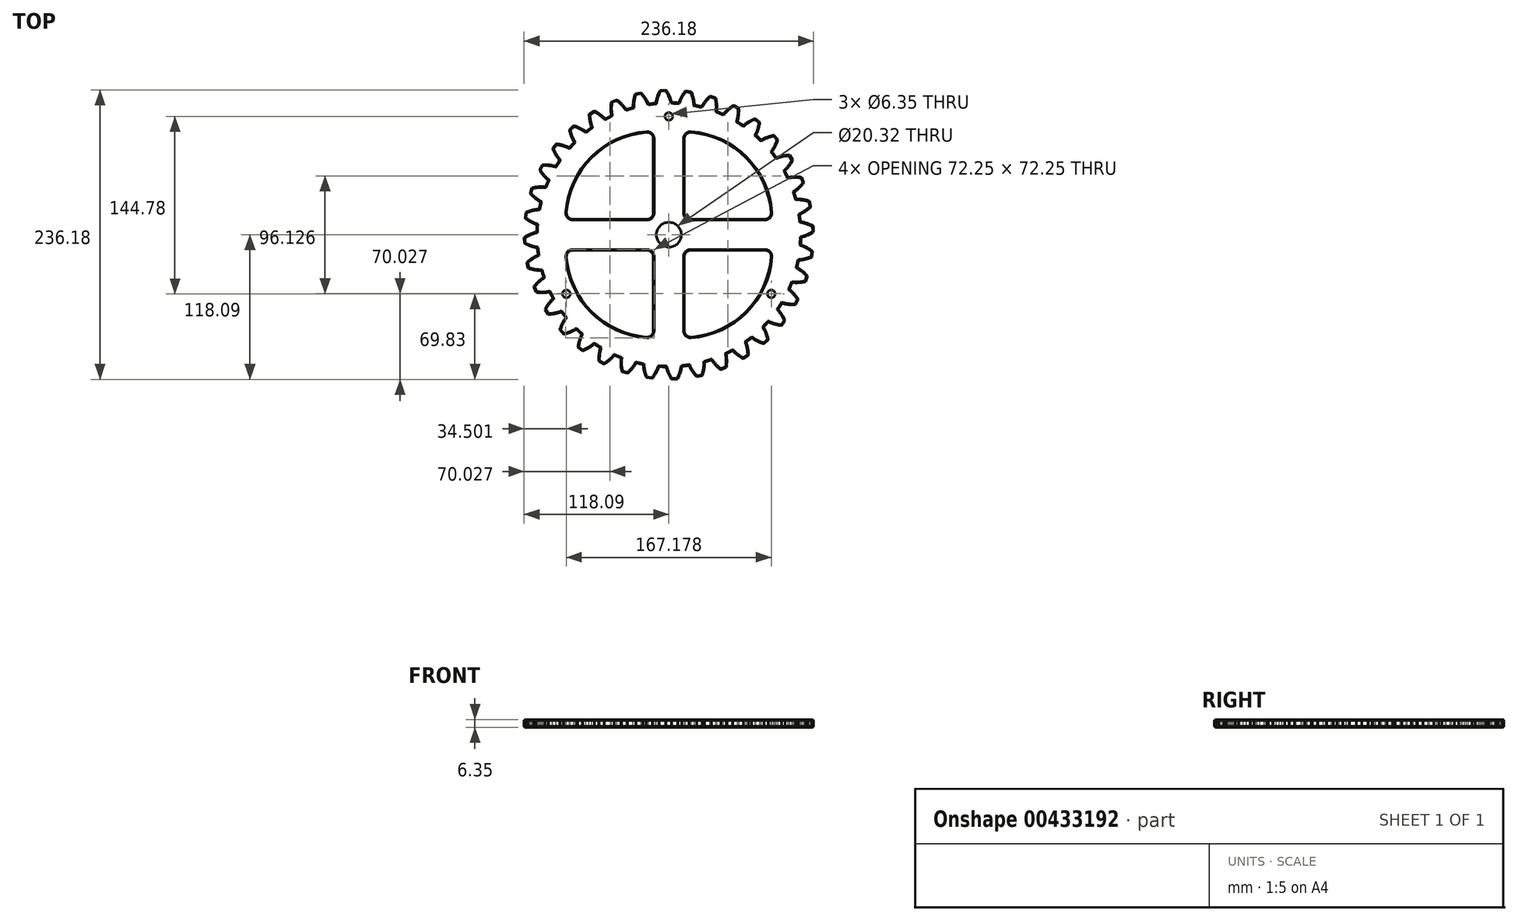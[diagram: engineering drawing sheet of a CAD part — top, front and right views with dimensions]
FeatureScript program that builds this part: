
annotation { "Feature Type Name" : "Feature", "Feature Type Description" : "" }
export const myFeature = defineFeature(function(context is Context, id is Id, definition is map)
    precondition{}
    {
        {
            var Q0;
            Q0=qCreatedBy(makeId("Top.planeOp"),FACE);
            var sketch = newSketch(context, id + "F0", { "sketchPlane" : qUnion([Q0])});
            skCircle(sketch, "E0", {"center": v(0, 0) * mm, "radius": 30.48 * mm, "construction": true});
            skSolve(sketch);
        }
        {
            var Q0;
            Q0=qCreatedBy(makeId("Top.planeOp"),FACE);
            var sketch = newSketch(context, id + "F1", { "sketchPlane" : qUnion([Q0])});
            skCircle(sketch, "E1", {"center": v(0, 0) * mm, "radius": 118.11 * mm, "construction": true});
            skCircle(sketch, "E2", {"center": v(0, 0) * mm, "radius": 114.3 * mm, "construction": true});
            skCircle(sketch, "E3", {"center": v(0, 0) * mm, "radius": 107.95 * mm, "construction": true});
            skLineSegment(sketch, "E4", {"start": v(0, 0) * mm, "end": v(0, 56.9) * mm, "construction": true});
            skLineSegment(sketch, "E5", {"start": v(0, 0) * mm, "end": v(-2.3, 58.79) * mm, "construction": true});
            skLineSegment(sketch, "E6", {"start": v(0, 114.3) * mm, "end": v(-65.71, 114.3) * mm, "construction": true});
            skLineSegment(sketch, "E7", {"start": v(0, 114.3) * mm, "end": v(-58.85, 88.1) * mm, "construction": true});
            skCircle(sketch, "E8", {"center": v(0, 114.3) * mm, "radius": 31.75 * mm, "construction": true});
            skCircle(sketch, "E9", {"center": v(0, 0) * mm, "radius": 104.42 * mm, "construction": true});
            skCircle(sketch, "E10", {"center": v(-28.56, 100.44) * mm, "radius": 31.75 * mm, "construction": true});
            skArc(sketch, "E11", {"start": v(2.3, 107.93) * mm, "mid": v(0.5, 113.2) * mm, "end": v(-2.17, 118.09) * mm});
            skArc(sketch, "E12.MirrorCS", {"start": v(-10.75, 107.41) * mm, "mid": v(-9.39, 112.82) * mm, "end": v(-7.1, 117.9) * mm});
            skLineSegment(sketch, "E13", {"start": v(-7.1, 117.9) * mm, "end": v(-2.17, 118.09) * mm});
            skArc(sketch, "E14", {"start": v(-10.75, 107.41) * mm, "mid": v(4.24, -107.87) * mm, "end": v(2.3, 107.93) * mm});
            skSolve(sketch);
        }
        {
            var Q0;
            Q0=qSketchRegion(id+"F1",true);
            var Q1;
            Q1=makeQuery(id+"Ffi0VH93psu6soF_0.opExtrude","CAP_FACE",FACE,{"disambiguationData":[OSD([sQuery(id+"F0.wireOp",EDGE,"E0")])],"isStart":true});
            extrude(context, id + "F2", {"entities" : qUnion([Q0]), "oppositeDirection" : true, "endBoundEntityFace" : qUnion([Q1]), "depth" : 6.35 * mm});
        }
        {
            var Q0;
            Q0=makeQuery(id+"F2.opExtrude","SWEPT_BODY",BODY,{"disambiguationData":[OSD([sQuery(id+"F1.wireOp",EDGE,"E11"),sQuery(id+"F1.wireOp",EDGE,"E12.MirrorCS"),sQuery(id+"F1.wireOp",EDGE,"E13"),sQuery(id+"F1.wireOp",EDGE,"ZPE7Z8ba-rLlS-d3gG-Tl0h-fifcE816pJjn")])]});
            var Q1;
            Q1=sQuery(id+"F0.wireOp",EDGE,"E0");
            circularPattern(context, id + "F3", {"operationType" : NewBodyOperationType.ADD, "entities" : qUnion([Q0]), "axis" : qUnion([Q1]), "angle" : 360 * degree, "instanceCount" : 36, "equalSpace" : true});
        }
        {
            var Q0;
            {var subQ0=makeQuery(id+"F2.opExtrude","CAP_FACE",FACE,{"disambiguationData":[OSD([sQuery(id+"F1.wireOp",EDGE,"E11"),sQuery(id+"F1.wireOp",EDGE,"E12.MirrorCS"),sQuery(id+"F1.wireOp",EDGE,"E13"),sQuery(id+"F1.wireOp",EDGE,"ZPE7Z8ba-rLlS-d3gG-Tl0h-fifcE816pJjn")])],"isStart":true});Q0=makeQuery(id+"F3.boolean.opBoolean","MERGE",FACE,{"derivedFrom":[makeQuery(id+"Ffi0VH93psu6soF_0.opExtrude","CAP_FACE",FACE,{"disambiguationData":[OSD([sQuery(id+"F0.wireOp",EDGE,"E0")])],"isStart":false}),subQ0,makeQuery(id+"F3.opPattern","COPY",FACE,{"derivedFrom":subQ0,"instanceName":"1"}),makeQuery(id+"F3.opPattern","COPY",FACE,{"derivedFrom":subQ0,"instanceName":"2"}),makeQuery(id+"F3.opPattern","COPY",FACE,{"derivedFrom":subQ0,"instanceName":"3"}),makeQuery(id+"F3.opPattern","COPY",FACE,{"derivedFrom":subQ0,"instanceName":"4"}),makeQuery(id+"F3.opPattern","COPY",FACE,{"derivedFrom":subQ0,"instanceName":"5"}),makeQuery(id+"F3.opPattern","COPY",FACE,{"derivedFrom":subQ0,"instanceName":"6"}),makeQuery(id+"F3.opPattern","COPY",FACE,{"derivedFrom":subQ0,"instanceName":"7"}),makeQuery(id+"F3.opPattern","COPY",FACE,{"derivedFrom":subQ0,"instanceName":"8"}),makeQuery(id+"F3.opPattern","COPY",FACE,{"derivedFrom":subQ0,"instanceName":"9"}),makeQuery(id+"F3.opPattern","COPY",FACE,{"derivedFrom":subQ0,"instanceName":"10"}),makeQuery(id+"F3.opPattern","COPY",FACE,{"derivedFrom":subQ0,"instanceName":"11"}),makeQuery(id+"F3.opPattern","COPY",FACE,{"derivedFrom":subQ0,"instanceName":"12"}),makeQuery(id+"F3.opPattern","COPY",FACE,{"derivedFrom":subQ0,"instanceName":"13"}),makeQuery(id+"F3.opPattern","COPY",FACE,{"derivedFrom":subQ0,"instanceName":"14"})]});}
            var sketch = newSketch(context, id + "F4", { "sketchPlane" : qUnion([Q0])});
            skLineSegment(sketch, "E15", {"start": v(-12.7, 12.7) * mm, "end": v(-83.64, 12.7) * mm});
            skLineSegment(sketch, "E16", {"start": v(-12.7, 12.7) * mm, "end": v(-12.7, 83.64) * mm});
            skArc(sketch, "E17", {"start": v(-12.7, 83.64) * mm, "mid": v(-62.86, 62.86) * mm, "end": v(-83.64, 12.7) * mm});
            skArc(sketch, "E18.1.0", {"start": v(-83.64, -12.7) * mm, "mid": v(-62.86, -62.86) * mm, "end": v(-12.7, -83.64) * mm});
            skLineSegment(sketch, "E18.1.1", {"start": v(-12.7, -12.7) * mm, "end": v(-83.64, -12.7) * mm});
            skLineSegment(sketch, "E18.1.2", {"start": v(-12.7, -12.7) * mm, "end": v(-12.7, -83.64) * mm});
            skArc(sketch, "E18.2.0", {"start": v(12.7, -83.64) * mm, "mid": v(62.86, -62.86) * mm, "end": v(83.64, -12.7) * mm});
            skLineSegment(sketch, "E18.2.1", {"start": v(12.7, -12.7) * mm, "end": v(12.7, -83.64) * mm});
            skLineSegment(sketch, "E18.2.2", {"start": v(12.7, -12.7) * mm, "end": v(83.64, -12.7) * mm});
            skArc(sketch, "E18.3.0", {"start": v(83.64, 12.7) * mm, "mid": v(62.86, 62.86) * mm, "end": v(12.7, 83.64) * mm});
            skLineSegment(sketch, "E18.3.1", {"start": v(12.7, 12.7) * mm, "end": v(83.64, 12.7) * mm});
            skLineSegment(sketch, "E18.3.2", {"start": v(12.7, 12.7) * mm, "end": v(12.7, 83.64) * mm});
            skPoint(sketch, "E18.center", {"position": v(0, 0) * mm});
            skSolve(sketch);
        }
        {
            var Q0;
            Q0=qSketchRegion(id+"F4",true);
            extrude(context, id + "F5", {"entities" : qUnion([Q0]), "operationType" : NewBodyOperationType.REMOVE, "endBound" : BoundingType.THROUGH_ALL, "oppositeDirection" : true, "depth" : 25.4 * mm});
        }
        {
            var Q0;
            Q0=makeQuery(id+"F5.boolean.opBoolean","COPY",EDGE,{"derivedFrom":makeQuery(id+"F5.opExtrude","SWEPT_EDGE",EDGE,{"disambiguationData":[OSD([sQuery(id+"F4.wireOp",EDGE,"E15"),sQuery(id+"F4.wireOp",EDGE,"E17")])]})});
            var Q1;
            Q1=makeQuery(id+"F5.boolean.opBoolean","COPY",EDGE,{"derivedFrom":makeQuery(id+"F5.opExtrude","SWEPT_EDGE",EDGE,{"disambiguationData":[OSD([sQuery(id+"F4.wireOp",EDGE,"E16"),sQuery(id+"F4.wireOp",EDGE,"E17")])]})});
            var Q2;
            Q2=makeQuery(id+"F5.boolean.opBoolean","COPY",EDGE,{"derivedFrom":makeQuery(id+"F5.opExtrude","SWEPT_EDGE",EDGE,{"disambiguationData":[OSD([sQuery(id+"F4.wireOp",EDGE,"E15"),sQuery(id+"F4.wireOp",EDGE,"E16")])]})});
            var Q3;
            Q3=makeQuery(id+"F5.boolean.opBoolean","COPY",EDGE,{"derivedFrom":makeQuery(id+"F5.opExtrude","SWEPT_EDGE",EDGE,{"disambiguationData":[OSD([sQuery(id+"F4.wireOp",EDGE,"E18.3.1"),sQuery(id+"F4.wireOp",EDGE,"E18.3.2")])]})});
            var Q4;
            Q4=makeQuery(id+"F5.boolean.opBoolean","COPY",EDGE,{"derivedFrom":makeQuery(id+"F5.opExtrude","SWEPT_EDGE",EDGE,{"disambiguationData":[OSD([sQuery(id+"F4.wireOp",EDGE,"E18.3.0"),sQuery(id+"F4.wireOp",EDGE,"E18.3.2")])]})});
            var Q5;
            Q5=makeQuery(id+"F5.boolean.opBoolean","COPY",EDGE,{"derivedFrom":makeQuery(id+"F5.opExtrude","SWEPT_EDGE",EDGE,{"disambiguationData":[OSD([sQuery(id+"F4.wireOp",EDGE,"E18.3.0"),sQuery(id+"F4.wireOp",EDGE,"E18.3.1")])]})});
            var Q6;
            Q6=makeQuery(id+"F5.boolean.opBoolean","COPY",EDGE,{"derivedFrom":makeQuery(id+"F5.opExtrude","SWEPT_EDGE",EDGE,{"disambiguationData":[OSD([sQuery(id+"F4.wireOp",EDGE,"E18.2.1"),sQuery(id+"F4.wireOp",EDGE,"E18.2.2")])]})});
            var Q7;
            Q7=makeQuery(id+"F5.boolean.opBoolean","COPY",EDGE,{"derivedFrom":makeQuery(id+"F5.opExtrude","SWEPT_EDGE",EDGE,{"disambiguationData":[OSD([sQuery(id+"F4.wireOp",EDGE,"E18.2.0"),sQuery(id+"F4.wireOp",EDGE,"E18.2.2")])]})});
            var Q8;
            Q8=makeQuery(id+"F5.boolean.opBoolean","COPY",EDGE,{"derivedFrom":makeQuery(id+"F5.opExtrude","SWEPT_EDGE",EDGE,{"disambiguationData":[OSD([sQuery(id+"F4.wireOp",EDGE,"E18.2.0"),sQuery(id+"F4.wireOp",EDGE,"E18.2.1")])]})});
            var Q9;
            Q9=makeQuery(id+"F5.boolean.opBoolean","COPY",EDGE,{"derivedFrom":makeQuery(id+"F5.opExtrude","SWEPT_EDGE",EDGE,{"disambiguationData":[OSD([sQuery(id+"F4.wireOp",EDGE,"E18.1.1"),sQuery(id+"F4.wireOp",EDGE,"E18.1.2")])]})});
            var Q10;
            Q10=makeQuery(id+"F5.boolean.opBoolean","COPY",EDGE,{"derivedFrom":makeQuery(id+"F5.opExtrude","SWEPT_EDGE",EDGE,{"disambiguationData":[OSD([sQuery(id+"F4.wireOp",EDGE,"E18.1.0"),sQuery(id+"F4.wireOp",EDGE,"E18.1.2")])]})});
            var Q11;
            Q11=makeQuery(id+"F5.boolean.opBoolean","COPY",EDGE,{"derivedFrom":makeQuery(id+"F5.opExtrude","SWEPT_EDGE",EDGE,{"disambiguationData":[OSD([sQuery(id+"F4.wireOp",EDGE,"E18.1.0"),sQuery(id+"F4.wireOp",EDGE,"E18.1.1")])]})});
            fillet(context, id + "F6", {"entities" : qUnion([Q0, Q1, Q2, Q3, Q4, Q5, Q6, Q7, Q8, Q9, Q10, Q11]), "radius" : 5.08 * mm, "tangentPropagation" : true, "allowEdgeOverflow" : false});
        }
        {
            var Q0;
            {var subQ0=makeQuery(id+"F2.opExtrude","CAP_FACE",FACE,{"disambiguationData":[OSD([sQuery(id+"F1.wireOp",EDGE,"E11"),sQuery(id+"F1.wireOp",EDGE,"E12.MirrorCS"),sQuery(id+"F1.wireOp",EDGE,"E13"),sQuery(id+"F1.wireOp",EDGE,"E14")])],"isStart":true});Q0=makeQuery(id+"F3.boolean.opBoolean","MERGE",FACE,{"derivedFrom":[subQ0,makeQuery(id+"F3.opPattern","COPY",FACE,{"derivedFrom":subQ0,"instanceName":"1"}),makeQuery(id+"F3.opPattern","COPY",FACE,{"derivedFrom":subQ0,"instanceName":"2"}),makeQuery(id+"F3.opPattern","COPY",FACE,{"derivedFrom":subQ0,"instanceName":"3"}),makeQuery(id+"F3.opPattern","COPY",FACE,{"derivedFrom":subQ0,"instanceName":"4"}),makeQuery(id+"F3.opPattern","COPY",FACE,{"derivedFrom":subQ0,"instanceName":"5"}),makeQuery(id+"F3.opPattern","COPY",FACE,{"derivedFrom":subQ0,"instanceName":"6"}),makeQuery(id+"F3.opPattern","COPY",FACE,{"derivedFrom":subQ0,"instanceName":"7"}),makeQuery(id+"F3.opPattern","COPY",FACE,{"derivedFrom":subQ0,"instanceName":"8"}),makeQuery(id+"F3.opPattern","COPY",FACE,{"derivedFrom":subQ0,"instanceName":"9"}),makeQuery(id+"F3.opPattern","COPY",FACE,{"derivedFrom":subQ0,"instanceName":"10"}),makeQuery(id+"F3.opPattern","COPY",FACE,{"derivedFrom":subQ0,"instanceName":"11"}),makeQuery(id+"F3.opPattern","COPY",FACE,{"derivedFrom":subQ0,"instanceName":"12"}),makeQuery(id+"F3.opPattern","COPY",FACE,{"derivedFrom":subQ0,"instanceName":"13"}),makeQuery(id+"F3.opPattern","COPY",FACE,{"derivedFrom":subQ0,"instanceName":"14"}),makeQuery(id+"F3.opPattern","COPY",FACE,{"derivedFrom":subQ0,"instanceName":"15"}),makeQuery(id+"F3.opPattern","COPY",FACE,{"derivedFrom":subQ0,"instanceName":"16"}),makeQuery(id+"F3.opPattern","COPY",FACE,{"derivedFrom":subQ0,"instanceName":"17"}),makeQuery(id+"F3.opPattern","COPY",FACE,{"derivedFrom":subQ0,"instanceName":"18"}),makeQuery(id+"F3.opPattern","COPY",FACE,{"derivedFrom":subQ0,"instanceName":"19"}),makeQuery(id+"F3.opPattern","COPY",FACE,{"derivedFrom":subQ0,"instanceName":"20"}),makeQuery(id+"F3.opPattern","COPY",FACE,{"derivedFrom":subQ0,"instanceName":"21"}),makeQuery(id+"F3.opPattern","COPY",FACE,{"derivedFrom":subQ0,"instanceName":"22"}),makeQuery(id+"F3.opPattern","COPY",FACE,{"derivedFrom":subQ0,"instanceName":"23"})]});}
            var Q1;
            {var subQ0=makeQuery(id+"F2.opExtrude","CAP_FACE",FACE,{"disambiguationData":[OSD([sQuery(id+"F1.wireOp",EDGE,"E11"),sQuery(id+"F1.wireOp",EDGE,"E12.MirrorCS"),sQuery(id+"F1.wireOp",EDGE,"E13"),sQuery(id+"F1.wireOp",EDGE,"E14")])],"isStart":false});Q1=makeQuery(id+"F3.boolean.opBoolean","MERGE",FACE,{"derivedFrom":[subQ0,makeQuery(id+"F3.opPattern","COPY",FACE,{"derivedFrom":subQ0,"instanceName":"1"}),makeQuery(id+"F3.opPattern","COPY",FACE,{"derivedFrom":subQ0,"instanceName":"2"}),makeQuery(id+"F3.opPattern","COPY",FACE,{"derivedFrom":subQ0,"instanceName":"3"}),makeQuery(id+"F3.opPattern","COPY",FACE,{"derivedFrom":subQ0,"instanceName":"4"}),makeQuery(id+"F3.opPattern","COPY",FACE,{"derivedFrom":subQ0,"instanceName":"5"}),makeQuery(id+"F3.opPattern","COPY",FACE,{"derivedFrom":subQ0,"instanceName":"6"}),makeQuery(id+"F3.opPattern","COPY",FACE,{"derivedFrom":subQ0,"instanceName":"7"}),makeQuery(id+"F3.opPattern","COPY",FACE,{"derivedFrom":subQ0,"instanceName":"8"}),makeQuery(id+"F3.opPattern","COPY",FACE,{"derivedFrom":subQ0,"instanceName":"9"}),makeQuery(id+"F3.opPattern","COPY",FACE,{"derivedFrom":subQ0,"instanceName":"10"}),makeQuery(id+"F3.opPattern","COPY",FACE,{"derivedFrom":subQ0,"instanceName":"11"}),makeQuery(id+"F3.opPattern","COPY",FACE,{"derivedFrom":subQ0,"instanceName":"12"}),makeQuery(id+"F3.opPattern","COPY",FACE,{"derivedFrom":subQ0,"instanceName":"13"}),makeQuery(id+"F3.opPattern","COPY",FACE,{"derivedFrom":subQ0,"instanceName":"14"}),makeQuery(id+"F3.opPattern","COPY",FACE,{"derivedFrom":subQ0,"instanceName":"15"}),makeQuery(id+"F3.opPattern","COPY",FACE,{"derivedFrom":subQ0,"instanceName":"16"}),makeQuery(id+"F3.opPattern","COPY",FACE,{"derivedFrom":subQ0,"instanceName":"17"}),makeQuery(id+"F3.opPattern","COPY",FACE,{"derivedFrom":subQ0,"instanceName":"18"}),makeQuery(id+"F3.opPattern","COPY",FACE,{"derivedFrom":subQ0,"instanceName":"19"}),makeQuery(id+"F3.opPattern","COPY",FACE,{"derivedFrom":subQ0,"instanceName":"20"}),makeQuery(id+"F3.opPattern","COPY",FACE,{"derivedFrom":subQ0,"instanceName":"21"}),makeQuery(id+"F3.opPattern","COPY",FACE,{"derivedFrom":subQ0,"instanceName":"22"}),makeQuery(id+"F3.opPattern","COPY",FACE,{"derivedFrom":subQ0,"instanceName":"23"})]});}
            chamfer(context, id + "F7", {"entities" : qUnion([Q0, Q1]), "width" : 0.76 * mm, "tangentPropagation" : true});
        }
        {
            var Q0;
            {var subQ0=makeQuery(id+"F2.opExtrude","CAP_FACE",FACE,{"disambiguationData":[OSD([sQuery(id+"F1.wireOp",EDGE,"E11"),sQuery(id+"F1.wireOp",EDGE,"E12.MirrorCS"),sQuery(id+"F1.wireOp",EDGE,"E13"),sQuery(id+"F1.wireOp",EDGE,"E14")])],"isStart":true});Q0=makeQuery(id+"F3.boolean.opBoolean","MERGE",FACE,{"derivedFrom":[subQ0,makeQuery(id+"F3.opPattern","COPY",FACE,{"derivedFrom":subQ0,"instanceName":"1"}),makeQuery(id+"F3.opPattern","COPY",FACE,{"derivedFrom":subQ0,"instanceName":"2"}),makeQuery(id+"F3.opPattern","COPY",FACE,{"derivedFrom":subQ0,"instanceName":"3"}),makeQuery(id+"F3.opPattern","COPY",FACE,{"derivedFrom":subQ0,"instanceName":"4"}),makeQuery(id+"F3.opPattern","COPY",FACE,{"derivedFrom":subQ0,"instanceName":"5"}),makeQuery(id+"F3.opPattern","COPY",FACE,{"derivedFrom":subQ0,"instanceName":"6"}),makeQuery(id+"F3.opPattern","COPY",FACE,{"derivedFrom":subQ0,"instanceName":"7"}),makeQuery(id+"F3.opPattern","COPY",FACE,{"derivedFrom":subQ0,"instanceName":"8"}),makeQuery(id+"F3.opPattern","COPY",FACE,{"derivedFrom":subQ0,"instanceName":"9"}),makeQuery(id+"F3.opPattern","COPY",FACE,{"derivedFrom":subQ0,"instanceName":"10"}),makeQuery(id+"F3.opPattern","COPY",FACE,{"derivedFrom":subQ0,"instanceName":"11"}),makeQuery(id+"F3.opPattern","COPY",FACE,{"derivedFrom":subQ0,"instanceName":"12"}),makeQuery(id+"F3.opPattern","COPY",FACE,{"derivedFrom":subQ0,"instanceName":"13"}),makeQuery(id+"F3.opPattern","COPY",FACE,{"derivedFrom":subQ0,"instanceName":"14"}),makeQuery(id+"F3.opPattern","COPY",FACE,{"derivedFrom":subQ0,"instanceName":"15"}),makeQuery(id+"F3.opPattern","COPY",FACE,{"derivedFrom":subQ0,"instanceName":"16"}),makeQuery(id+"F3.opPattern","COPY",FACE,{"derivedFrom":subQ0,"instanceName":"17"}),makeQuery(id+"F3.opPattern","COPY",FACE,{"derivedFrom":subQ0,"instanceName":"18"}),makeQuery(id+"F3.opPattern","COPY",FACE,{"derivedFrom":subQ0,"instanceName":"19"}),makeQuery(id+"F3.opPattern","COPY",FACE,{"derivedFrom":subQ0,"instanceName":"20"}),makeQuery(id+"F3.opPattern","COPY",FACE,{"derivedFrom":subQ0,"instanceName":"21"}),makeQuery(id+"F3.opPattern","COPY",FACE,{"derivedFrom":subQ0,"instanceName":"22"}),makeQuery(id+"F3.opPattern","COPY",FACE,{"derivedFrom":subQ0,"instanceName":"23"})]});}
            var sketch = newSketch(context, id + "F8", { "sketchPlane" : qUnion([Q0])});
            skCircle(sketch, "E19", {"center": v(0, 0) * mm, "radius": 10.16 * mm});
            skSolve(sketch);
        }
        {
            var Q0;
            Q0=qSketchRegion(id+"F8",true);
            extrude(context, id + "F9", {"entities" : qUnion([Q0]), "operationType" : NewBodyOperationType.REMOVE, "oppositeDirection" : true, "depth" : 19.05 * mm});
        }
        {
            var Q0;
            {var subQ0=makeQuery(id+"F2.opExtrude","CAP_FACE",FACE,{"disambiguationData":[OSD([sQuery(id+"F1.wireOp",EDGE,"E11"),sQuery(id+"F1.wireOp",EDGE,"E12.MirrorCS"),sQuery(id+"F1.wireOp",EDGE,"E13"),sQuery(id+"F1.wireOp",EDGE,"E14")])],"isStart":true});Q0=makeQuery(id+"F3.boolean.opBoolean","MERGE",FACE,{"derivedFrom":[subQ0,makeQuery(id+"F3.opPattern","COPY",FACE,{"derivedFrom":subQ0,"instanceName":"1"}),makeQuery(id+"F3.opPattern","COPY",FACE,{"derivedFrom":subQ0,"instanceName":"2"}),makeQuery(id+"F3.opPattern","COPY",FACE,{"derivedFrom":subQ0,"instanceName":"3"}),makeQuery(id+"F3.opPattern","COPY",FACE,{"derivedFrom":subQ0,"instanceName":"4"}),makeQuery(id+"F3.opPattern","COPY",FACE,{"derivedFrom":subQ0,"instanceName":"5"}),makeQuery(id+"F3.opPattern","COPY",FACE,{"derivedFrom":subQ0,"instanceName":"6"}),makeQuery(id+"F3.opPattern","COPY",FACE,{"derivedFrom":subQ0,"instanceName":"7"}),makeQuery(id+"F3.opPattern","COPY",FACE,{"derivedFrom":subQ0,"instanceName":"8"}),makeQuery(id+"F3.opPattern","COPY",FACE,{"derivedFrom":subQ0,"instanceName":"9"}),makeQuery(id+"F3.opPattern","COPY",FACE,{"derivedFrom":subQ0,"instanceName":"10"}),makeQuery(id+"F3.opPattern","COPY",FACE,{"derivedFrom":subQ0,"instanceName":"11"}),makeQuery(id+"F3.opPattern","COPY",FACE,{"derivedFrom":subQ0,"instanceName":"12"}),makeQuery(id+"F3.opPattern","COPY",FACE,{"derivedFrom":subQ0,"instanceName":"13"}),makeQuery(id+"F3.opPattern","COPY",FACE,{"derivedFrom":subQ0,"instanceName":"14"}),makeQuery(id+"F3.opPattern","COPY",FACE,{"derivedFrom":subQ0,"instanceName":"15"}),makeQuery(id+"F3.opPattern","COPY",FACE,{"derivedFrom":subQ0,"instanceName":"16"}),makeQuery(id+"F3.opPattern","COPY",FACE,{"derivedFrom":subQ0,"instanceName":"17"}),makeQuery(id+"F3.opPattern","COPY",FACE,{"derivedFrom":subQ0,"instanceName":"18"}),makeQuery(id+"F3.opPattern","COPY",FACE,{"derivedFrom":subQ0,"instanceName":"19"}),makeQuery(id+"F3.opPattern","COPY",FACE,{"derivedFrom":subQ0,"instanceName":"20"}),makeQuery(id+"F3.opPattern","COPY",FACE,{"derivedFrom":subQ0,"instanceName":"21"}),makeQuery(id+"F3.opPattern","COPY",FACE,{"derivedFrom":subQ0,"instanceName":"22"}),makeQuery(id+"F3.opPattern","COPY",FACE,{"derivedFrom":subQ0,"instanceName":"23"}),makeQuery(id+"F3.opPattern","COPY",FACE,{"derivedFrom":subQ0,"instanceName":"24"}),makeQuery(id+"F3.opPattern","COPY",FACE,{"derivedFrom":subQ0,"instanceName":"25"}),makeQuery(id+"F3.opPattern","COPY",FACE,{"derivedFrom":subQ0,"instanceName":"26"}),makeQuery(id+"F3.opPattern","COPY",FACE,{"derivedFrom":subQ0,"instanceName":"27"}),makeQuery(id+"F3.opPattern","COPY",FACE,{"derivedFrom":subQ0,"instanceName":"28"}),makeQuery(id+"F3.opPattern","COPY",FACE,{"derivedFrom":subQ0,"instanceName":"29"}),makeQuery(id+"F3.opPattern","COPY",FACE,{"derivedFrom":subQ0,"instanceName":"30"}),makeQuery(id+"F3.opPattern","COPY",FACE,{"derivedFrom":subQ0,"instanceName":"31"}),makeQuery(id+"F3.opPattern","COPY",FACE,{"derivedFrom":subQ0,"instanceName":"32"}),makeQuery(id+"F3.opPattern","COPY",FACE,{"derivedFrom":subQ0,"instanceName":"33"}),makeQuery(id+"F3.opPattern","COPY",FACE,{"derivedFrom":subQ0,"instanceName":"34"}),makeQuery(id+"F3.opPattern","COPY",FACE,{"derivedFrom":subQ0,"instanceName":"35"})]});}
            var sketch = newSketch(context, id + "F10", { "sketchPlane" : qUnion([Q0])});
            skCircle(sketch, "E20", {"center": v(0, 96.52) * mm, "radius": 3.18 * mm});
            skCircle(sketch, "E21.1.0", {"center": v(-83.59, -48.26) * mm, "radius": 3.18 * mm});
            skCircle(sketch, "E21.2.0", {"center": v(83.59, -48.26) * mm, "radius": 3.18 * mm});
            skPoint(sketch, "E21.center", {"position": v(0, 0) * mm});
            skSolve(sketch);
        }
        {
            var Q0;
            Q0 = qSketchRegion(id + "F10", true);
            extrude(context, id + "F11", {"entities" : qUnion([Q0]), "operationType" : NewBodyOperationType.REMOVE, "endBound" : BoundingType.THROUGH_ALL, "oppositeDirection" : true, "depth" : 25.4 * mm});
        }
    });
